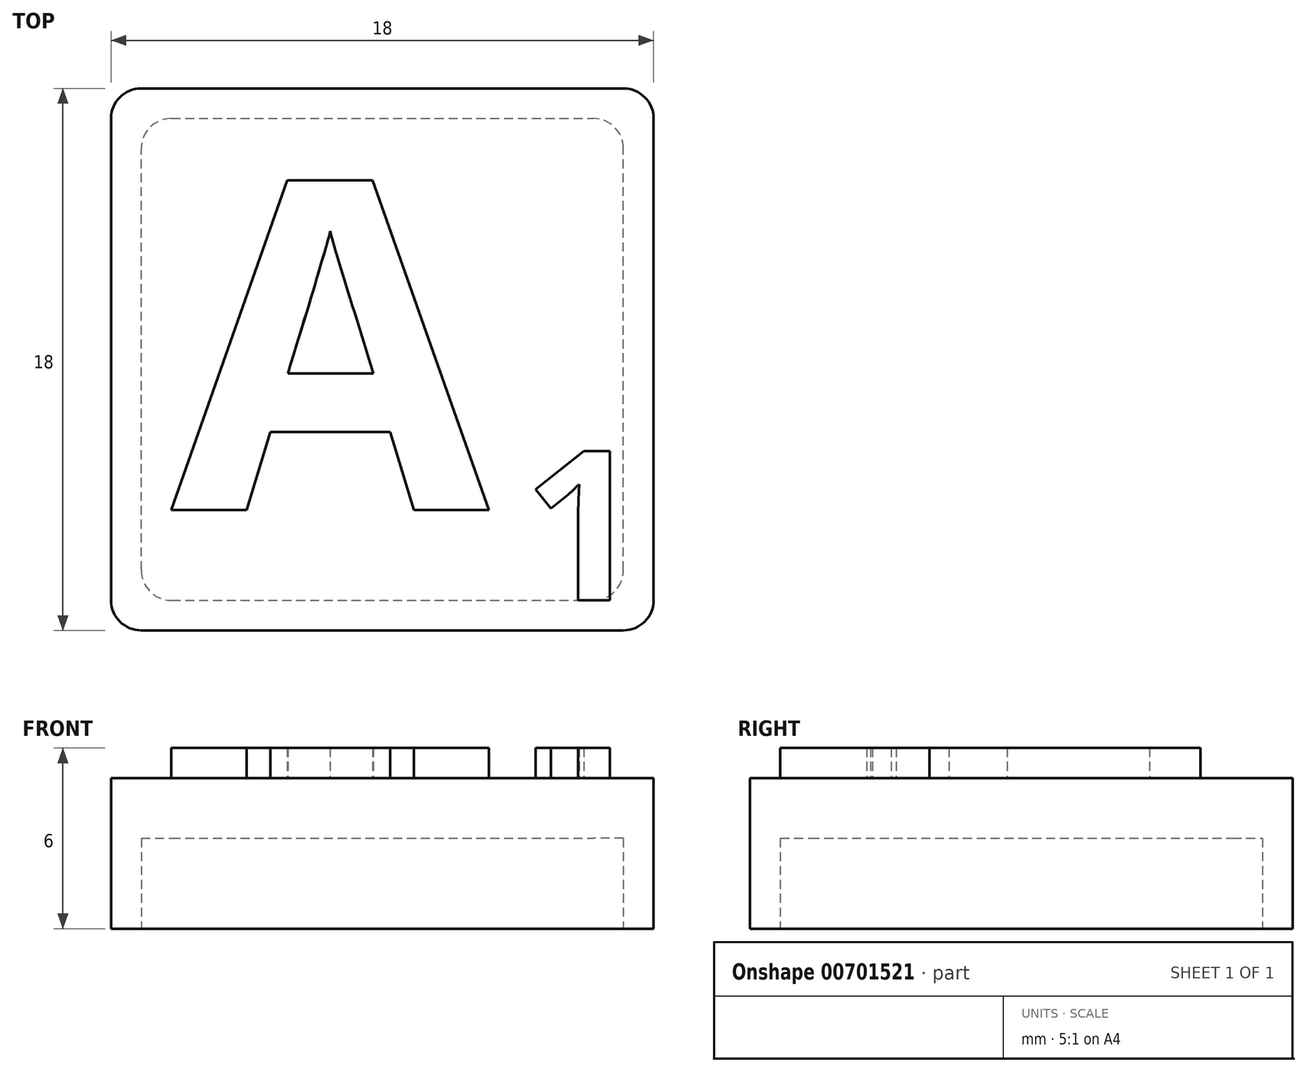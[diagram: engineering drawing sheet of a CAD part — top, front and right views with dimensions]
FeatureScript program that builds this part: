
annotation { "Feature Type Name" : "Feature", "Feature Type Description" : "" }
export const myFeature = defineFeature(function(context is Context, id is Id, definition is map)
    precondition{}
    {
        {
            var Q0;
            Q0=qCreatedBy(makeId("Top.planeOp"),FACE);
            var sketch = newSketch(context, id + "F0", { "sketchPlane" : qUnion([Q0])});
            skLineSegment(sketch, "E0.bottom", {"start": v(-3.93, 7.24) * mm, "end": v(14.07, 7.24) * mm});
            skLineSegment(sketch, "E0.top", {"start": v(-3.93, -10.76) * mm, "end": v(14.07, -10.76) * mm});
            skLineSegment(sketch, "E0.left", {"start": v(-3.93, 7.24) * mm, "end": v(-3.93, -10.76) * mm});
            skLineSegment(sketch, "E0.right", {"start": v(14.07, 7.24) * mm, "end": v(14.07, -10.76) * mm});
            skSolve(sketch);
        }
        {
            var Q0;
            Q0 = qSketchRegion(id + "F0", true);
            extrude(context, id + "F1", {"entities" : qUnion([Q0]), "depth" : 5 * mm, "offsetDistance" : 25 * mm});
        }
        {
            var Q0;
            Q0=qCreatedBy(makeId("Top.planeOp"),FACE);
            var sketch = newSketch(context, id + "F2", { "sketchPlane" : qUnion([Q0])});
            skLineSegment(sketch, "E1.bottom", {"start": v(-2.93, -9.76) * mm, "end": v(13.07, -9.76) * mm});
            skLineSegment(sketch, "E1.top", {"start": v(-2.93, 6.24) * mm, "end": v(13.07, 6.24) * mm});
            skLineSegment(sketch, "E1.left", {"start": v(-2.93, -9.76) * mm, "end": v(-2.93, 6.24) * mm});
            skLineSegment(sketch, "E1.right", {"start": v(13.07, -9.76) * mm, "end": v(13.07, 6.24) * mm});
            skSolve(sketch);
        }
        {
            var Q0;
            Q0=makeQuery(id+"F2.imprint","IMPRINT",FACE,{"disambiguationData":[TD([[makeQuery(id+"F2.imprint","IMPRINT",EDGE,{"derivedFrom":sQuery(id+"F2.wireOp",EDGE,"E1.bottom")}),1.0]])]});
            extrude(context, id + "F3", {"entities" : qUnion([Q0]), "operationType" : NewBodyOperationType.REMOVE, "depth" : 3 * mm, "offsetDistance" : 25 * mm});
        }
        {
            var Q0;
            Q0=makeQuery(id+"F1.opExtrude","CAP_FACE",FACE,{"disambiguationData":[OSD([sQuery(id+"F0.wireOp",EDGE,"E0.bottom"),sQuery(id+"F0.wireOp",EDGE,"E0.top"),sQuery(id+"F0.wireOp",EDGE,"E0.left"),sQuery(id+"F0.wireOp",EDGE,"E0.right")])],"isStart":false});
            var sketch = newSketch(context, id + "F4", { "sketchPlane" : qUnion([Q0])});
            skText(sketch, "E2", { "text": "A", "fontName": "OpenSans-Bold.ttf"});
            skText(sketch, "E3", { "text": "1", "fontName": "OpenSans-Bold.ttf"});
            const initialGuessF4  = {"E2": [-0.00193, -0.00676, 1, 0, 0.011], "E3": [0.00975, -0.00976, 1, 0, 0.005]};
            skSetInitialGuess(sketch, initialGuessF4);
            skSolve(sketch);
        }
        {
            var Q0;
            Q0=makeQuery(id+"F4.imprint","IMPRINT",FACE,{"disambiguationData":[TD([[makeQuery(id+"F4.imprint","IMPRINT",EDGE,{"derivedFrom":sQuery(id+"F4.wireOp",EDGE,"E2.sketch_text.stroke-0")}),-1.0]])]});
            var Q1;
            Q1=makeQuery(id+"F4.imprint","IMPRINT",FACE,{"disambiguationData":[TD([[makeQuery(id+"F4.imprint","IMPRINT",EDGE,{"derivedFrom":sQuery(id+"F4.wireOp",EDGE,"E3.sketch_text.stroke-0")}),-1.0]])]});
            extrude(context, id + "F5", {"entities" : qUnion([Q0, Q1]), "operationType" : NewBodyOperationType.ADD, "depth" : 1 * mm, "offsetDistance" : 25 * mm});
        }
        {
            var Q0;
            Q0=makeQuery(id+"F1.opExtrude","SWEPT_EDGE",EDGE,{"disambiguationData":[OSD([sQuery(id+"F0.wireOp",EDGE,"E0.bottom"),sQuery(id+"F0.wireOp",EDGE,"E0.right")])]});
            var Q1;
            Q1=makeQuery(id+"F1.opExtrude","SWEPT_EDGE",EDGE,{"disambiguationData":[OSD([sQuery(id+"F0.wireOp",EDGE,"E0.top"),sQuery(id+"F0.wireOp",EDGE,"E0.right")])]});
            var Q2;
            Q2=makeQuery(id+"F1.opExtrude","SWEPT_EDGE",EDGE,{"disambiguationData":[OSD([sQuery(id+"F0.wireOp",EDGE,"E0.top"),sQuery(id+"F0.wireOp",EDGE,"E0.left")])]});
            var Q3;
            Q3=makeQuery(id+"F1.opExtrude","SWEPT_EDGE",EDGE,{"disambiguationData":[OSD([sQuery(id+"F0.wireOp",EDGE,"E0.bottom"),sQuery(id+"F0.wireOp",EDGE,"E0.left")])]});
            var Q4;
            Q4=makeQuery(id+"F3.boolean.opBoolean","COPY",EDGE,{"derivedFrom":makeQuery(id+"F3.opExtrude","SWEPT_EDGE",EDGE,{"disambiguationData":[OSD([sQuery(id+"F2.wireOp",EDGE,"E1.bottom"),sQuery(id+"F2.wireOp",EDGE,"E1.right")])]})});
            var Q5;
            Q5=makeQuery(id+"F3.boolean.opBoolean","COPY",EDGE,{"derivedFrom":makeQuery(id+"F3.opExtrude","SWEPT_EDGE",EDGE,{"disambiguationData":[OSD([sQuery(id+"F2.wireOp",EDGE,"E1.bottom"),sQuery(id+"F2.wireOp",EDGE,"E1.left")])]})});
            var Q6;
            Q6=makeQuery(id+"F3.boolean.opBoolean","COPY",EDGE,{"derivedFrom":makeQuery(id+"F3.opExtrude","SWEPT_EDGE",EDGE,{"disambiguationData":[OSD([sQuery(id+"F2.wireOp",EDGE,"E1.top"),sQuery(id+"F2.wireOp",EDGE,"E1.left")])]})});
            var Q7;
            Q7=makeQuery(id+"F3.boolean.opBoolean","COPY",EDGE,{"derivedFrom":makeQuery(id+"F3.opExtrude","SWEPT_EDGE",EDGE,{"disambiguationData":[OSD([sQuery(id+"F2.wireOp",EDGE,"E1.top"),sQuery(id+"F2.wireOp",EDGE,"E1.right")])]})});
            fillet(context, id + "F6", {"entities" : qUnion([Q0, Q1, Q2, Q3, Q4, Q5, Q6, Q7]), "radius" : 1 * mm, "tangentPropagation" : true, "allowEdgeOverflow" : false});
        }
    });
